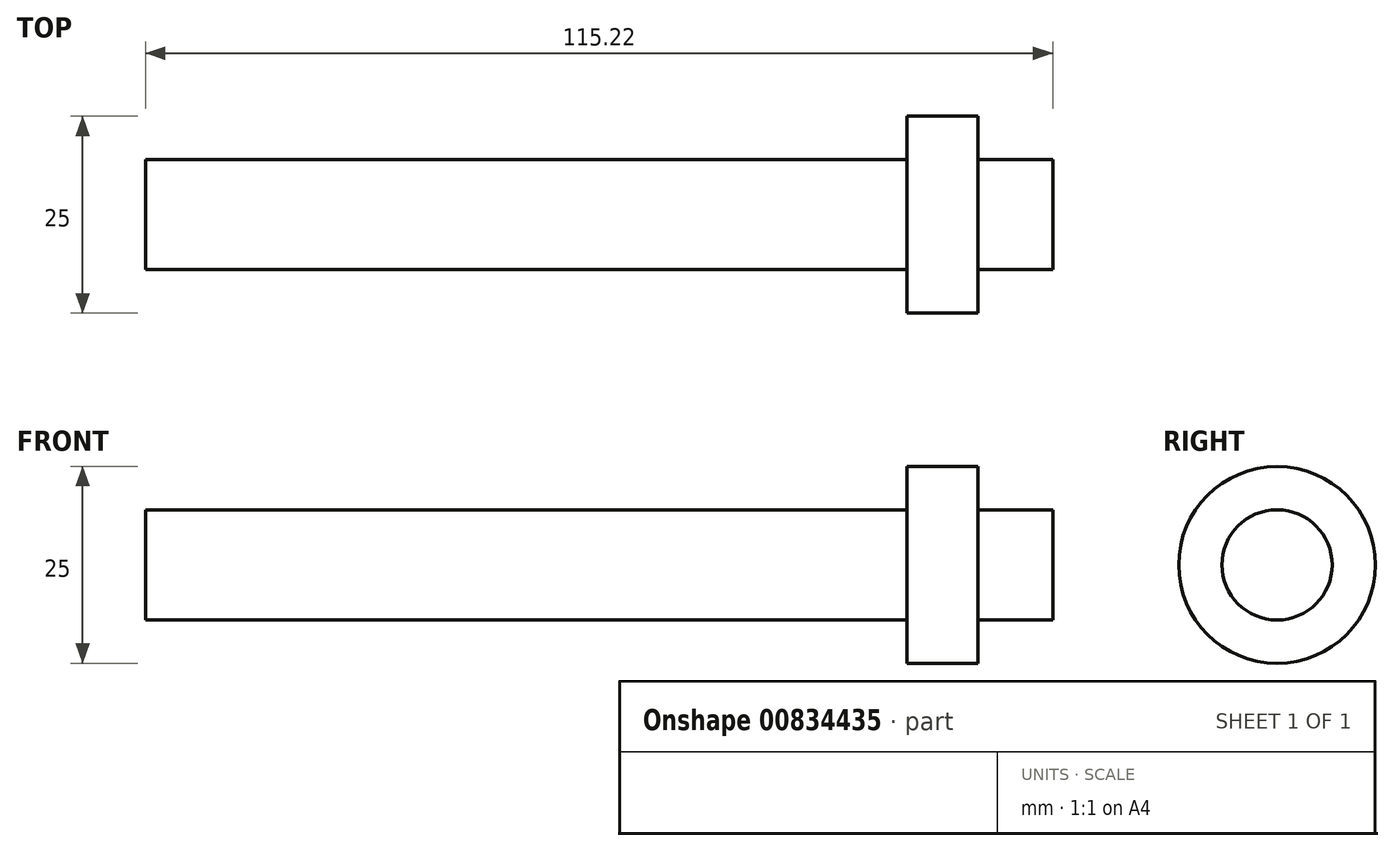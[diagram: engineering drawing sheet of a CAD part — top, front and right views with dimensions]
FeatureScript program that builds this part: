
annotation { "Feature Type Name" : "Feature", "Feature Type Description" : "" }
export const myFeature = defineFeature(function(context is Context, id is Id, definition is map)
    precondition{}
    {
        {
            var Q0;
            Q0=qCreatedBy(makeId("Front.planeOp"),FACE);
            var sketch = newSketch(context, id + "F0", { "sketchPlane" : qUnion([Q0])});
            skLineSegment(sketch, "E0", {"start": v(0, 0) * mm, "end": v(-96.46, 0) * mm});
            skPoint(sketch, "E1", {"position": v(-50.23, 0) * mm});
            skLineSegment(sketch, "E2", {"start": v(0, 0) * mm, "end": v(55.5, 0) * mm});
            skLineSegment(sketch, "E3", {"start": v(-50.23, 0) * mm, "end": v(-50.23, 7) * mm});
            skLineSegment(sketch, "E4", {"start": v(49.47, 42.7) * mm, "end": v(49.47, 47.7) * mm});
            skLineSegment(sketch, "E5", {"start": v(49.47, 47.7) * mm, "end": v(44.47, 47.7) * mm});
            skLineSegment(sketch, "E6", {"start": v(44.47, 47.7) * mm, "end": v(44.47, 39.3) * mm});
            skLineSegment(sketch, "E7", {"start": v(40.47, 41.34) * mm, "end": v(40.47, 59.89) * mm});
            skLineSegment(sketch, "E8", {"start": v(-50.23, 18.95) * mm, "end": v(-96.46, 18.95) * mm});
            skLineSegment(sketch, "E9", {"start": v(-96.46, 18.95) * mm, "end": v(-96.46, 0) * mm});
            skLineSegment(sketch, "E10", {"start": v(40.47, 41.34) * mm, "end": v(40.47, 39.93) * mm});
            skArc(sketch, "E11", {"start": v(40.47, 59.89) * mm, "mid": v(38.78, 61.75) * mm, "end": v(36.97, 60) * mm});
            skLineSegment(sketch, "E12", {"start": v(-40.04, 18.25) * mm, "end": v(2.55, 28.06) * mm});
            skLineSegment(sketch, "E13", {"start": v(42.92, 37.35) * mm, "end": v(43.06, 37.39) * mm});
            skLineSegment(sketch, "E14", {"start": v(-50.23, 18.95) * mm, "end": v(-45.23, 60) * mm});
            skPoint(sketch, "E15.center.orphan", {"position": v(-43.48, 60) * mm});
            skLineSegment(sketch, "E16", {"start": v(-45.23, 60) * mm, "end": v(-41.75, 59.58) * mm});
            skLineSegment(sketch, "E17", {"start": v(-41.75, 59.58) * mm, "end": v(-46.12, 23.73) * mm});
            skLineSegment(sketch, "E18", {"start": v(2.55, 28.06) * mm, "end": v(33.1, 35.1) * mm});
            skLineSegment(sketch, "E19", {"start": v(2.55, 28.06) * mm, "end": v(2.55, 28.06) * mm});
            skLineSegment(sketch, "E20", {"start": v(2.48, 28.04) * mm, "end": v(1.54, 308.97) * mm});
            skLineSegment(sketch, "E21", {"start": v(2.48, 28.04) * mm, "end": v(2.47, 28.38) * mm});
            skLineSegment(sketch, "E22", {"start": v(1.54, 308.97) * mm, "end": v(-20.46, 308.97) * mm});
            skLineSegment(sketch, "E23", {"start": v(-20.46, 308.97) * mm, "end": v(-20.46, 272.68) * mm});
            skLineSegment(sketch, "E24", {"start": v(-20.46, 272.68) * mm, "end": v(1.54, 272.68) * mm});
            skLineSegment(sketch, "E25", {"start": v(36.97, 60) * mm, "end": v(36.97, 39.96) * mm});
            skLineSegment(sketch, "E26", {"start": v(40.47, 39.93) * mm, "end": v(40.47, 39.3) * mm});
            skPoint(sketch, "E27.visualSharp", {"position": v(-46.98, 16.65) * mm});
            skArc(sketch, "E27.filletArc", {"start": v(-46.12, 23.73) * mm, "mid": v(-44.5, 19.4) * mm, "end": v(-40.04, 18.25) * mm});
            skLineSegment(sketch, "E28", {"start": v(63.54, 38) * mm, "end": v(63.54, 42.7) * mm});
            skLineSegment(sketch, "E29", {"start": v(49.47, 42.7) * mm, "end": v(63.54, 42.7) * mm});
            skPoint(sketch, "E30.orphan", {"position": v(49.47, 37.7) * mm});
            skPoint(sketch, "E31.visualSharp", {"position": v(36.97, 35.98) * mm});
            skArc(sketch, "E31.filletArc", {"start": v(33.1, 35.1) * mm, "mid": v(35.88, 36.85) * mm, "end": v(36.97, 39.96) * mm});
            skPoint(sketch, "E32.visualSharp", {"position": v(40.47, 36.8) * mm});
            skArc(sketch, "E32.filletArc", {"start": v(40.47, 39.3) * mm, "mid": v(41.22, 37.74) * mm, "end": v(42.92, 37.35) * mm});
            skPoint(sketch, "E33.visualSharp", {"position": v(44.47, 37.71) * mm});
            skArc(sketch, "E33.filletArc", {"start": v(42.92, 37.35) * mm, "mid": v(44.03, 38.06) * mm, "end": v(44.47, 39.3) * mm});
            skLineSegment(sketch, "E34", {"start": v(65.5, 32.87) * mm, "end": v(66.58, 32.87) * mm});
            skLineSegment(sketch, "E35", {"start": v(65.5, 32.87) * mm, "end": v(65.5, 12.5) * mm});
            skArc(sketch, "E36", {"start": v(14.12, 21.05) * mm, "mid": v(16.07, 21.85) * mm, "end": v(16.87, 23.8) * mm});
            skArc(sketch, "E37", {"start": v(-11.53, 20.95) * mm, "mid": v(-13.2, 19.9) * mm, "end": v(-13.86, 18.03) * mm});
            skArc(sketch, "E38", {"start": v(57.8, 29.58) * mm, "mid": v(60.27, 30.6) * mm, "end": v(61.3, 33.08) * mm});
            skLineSegment(sketch, "E39", {"start": v(54.3, 33.08) * mm, "end": v(45.43, 33.83) * mm});
            skPoint(sketch, "E40.orphan", {"position": v(14.12, 21.03) * mm});
            skLineSegment(sketch, "E41", {"start": v(11.37, 23.8) * mm, "end": v(0.81, 23.8) * mm});
            skArc(sketch, "E42.trimOffspring", {"start": v(-10.86, 15.03) * mm, "mid": v(-8.74, 15.9) * mm, "end": v(-7.86, 18.03) * mm});
            skArc(sketch, "E43.trimOffspring", {"start": v(13.5, 26.48) * mm, "mid": v(11.97, 25.5) * mm, "end": v(11.37, 23.8) * mm});
            skLineSegment(sketch, "E44", {"start": v(57.8, 29.58) * mm, "end": v(16.87, 23.8) * mm});
            skArc(sketch, "E45.trimOffspring", {"start": v(57, 36.5) * mm, "mid": v(55.05, 35.26) * mm, "end": v(54.3, 33.08) * mm});
            skLineSegment(sketch, "E46", {"start": v(61.3, 33.08) * mm, "end": v(65.5, 32.87) * mm});
            skPoint(sketch, "E47.start.orphan", {"position": v(16.87, 21.03) * mm});
            skPoint(sketch, "E48.end.orphan", {"position": v(61.3, 29.58) * mm});
            skLineSegment(sketch, "E49.trimOffspring", {"start": v(57, 36.5) * mm, "end": v(63.54, 38) * mm});
            skLineSegment(sketch, "E50.trimOffspring", {"start": v(13.5, 26.48) * mm, "end": v(45.43, 33.83) * mm});
            skLineSegment(sketch, "E51.trimOffspring", {"start": v(-11.53, 20.95) * mm, "end": v(0.81, 23.8) * mm});
            skLineSegment(sketch, "E52", {"start": v(-43.23, 7) * mm, "end": v(-50.23, 7) * mm});
            skPoint(sketch, "E53.orphan", {"position": v(-50.23, 11.8) * mm});
            skLineSegment(sketch, "E54.trimOffspring", {"start": v(-50.23, 18.95) * mm, "end": v(-50.23, 103.76) * mm});
            skLineSegment(sketch, "E55", {"start": v(-43.23, 7) * mm, "end": v(45.5, 7) * mm});
            skArc(sketch, "E56", {"start": v(-41.24, 14.44) * mm, "mid": v(-42.67, 13.57) * mm, "end": v(-43.23, 12) * mm});
            skLineSegment(sketch, "E57", {"start": v(-43.23, 7) * mm, "end": v(-43.23, 12) * mm});
            skLineSegment(sketch, "E58", {"start": v(-40.73, 9.5) * mm, "end": v(-40.73, 7) * mm});
            skLineSegment(sketch, "E59", {"start": v(-38.24, 12.25) * mm, "end": v(-10.86, 15.03) * mm});
            skArc(sketch, "E60.trimOffspring", {"start": v(-40.73, 9.5) * mm, "mid": v(-38.87, 10.32) * mm, "end": v(-38.24, 12.25) * mm});
            skLineSegment(sketch, "E61", {"start": v(-7.86, 18.03) * mm, "end": v(14.12, 21.05) * mm});
            skLineSegment(sketch, "E62", {"start": v(-41.24, 14.44) * mm, "end": v(-13.86, 18.03) * mm});
            skLineSegment(sketch, "E63", {"start": v(45.5, 7) * mm, "end": v(45.5, 12.5) * mm});
            skLineSegment(sketch, "E64", {"start": v(55.5, 12.5) * mm, "end": v(45.5, 12.5) * mm});
            skLineSegment(sketch, "E65", {"start": v(65.5, 12.5) * mm, "end": v(55.5, 12.5) * mm});
            skLineSegment(sketch, "E66", {"start": v(55.5, 12.5) * mm, "end": v(55.5, 7) * mm});
            skLineSegment(sketch, "E67", {"start": v(55.5, 7) * mm, "end": v(65, 7) * mm});
            skLineSegment(sketch, "E68", {"start": v(64.5, 12.5) * mm, "end": v(64.5, 7) * mm});
            skLineSegment(sketch, "E69", {"start": v(46.5, 12.5) * mm, "end": v(46.5, 7) * mm});
            skLineSegment(sketch, "E70", {"start": v(65, 7) * mm, "end": v(65, 0) * mm});
            skLineSegment(sketch, "E71", {"start": v(65, 0) * mm, "end": v(55.5, 0) * mm});
            skLineSegment(sketch, "E72", {"start": v(45.5, 7) * mm, "end": v(46.5, 7) * mm});
            skPoint(sketch, "E73.end.orphan", {"position": v(46.5, 0) * mm});
            skSolve(sketch);
        }
        {
            var Q0;
            {var subQ7=sQuery(id+"F0.wireOp",EDGE,"E2");Q0=makeQuery(id+"F0.imprint","IMPRINT",FACE,{"disambiguationData":[TD([[makeQuery(id+"F0.imprint","IMPRINT",EDGE,{"derivedFrom":subQ7}),1.0]])]});}
            var Q1;
            Q1=sQuery(id+"F0.wireOp",EDGE,"E2");
            revolve(context, id + "F1", {"surfaceOperationType" : NewSurfaceOperationType.NEW, "entities" : qUnion([Q0]), "axis" : qUnion([Q1]), "revolveType" : RevolveType.FULL});
        }
    });
